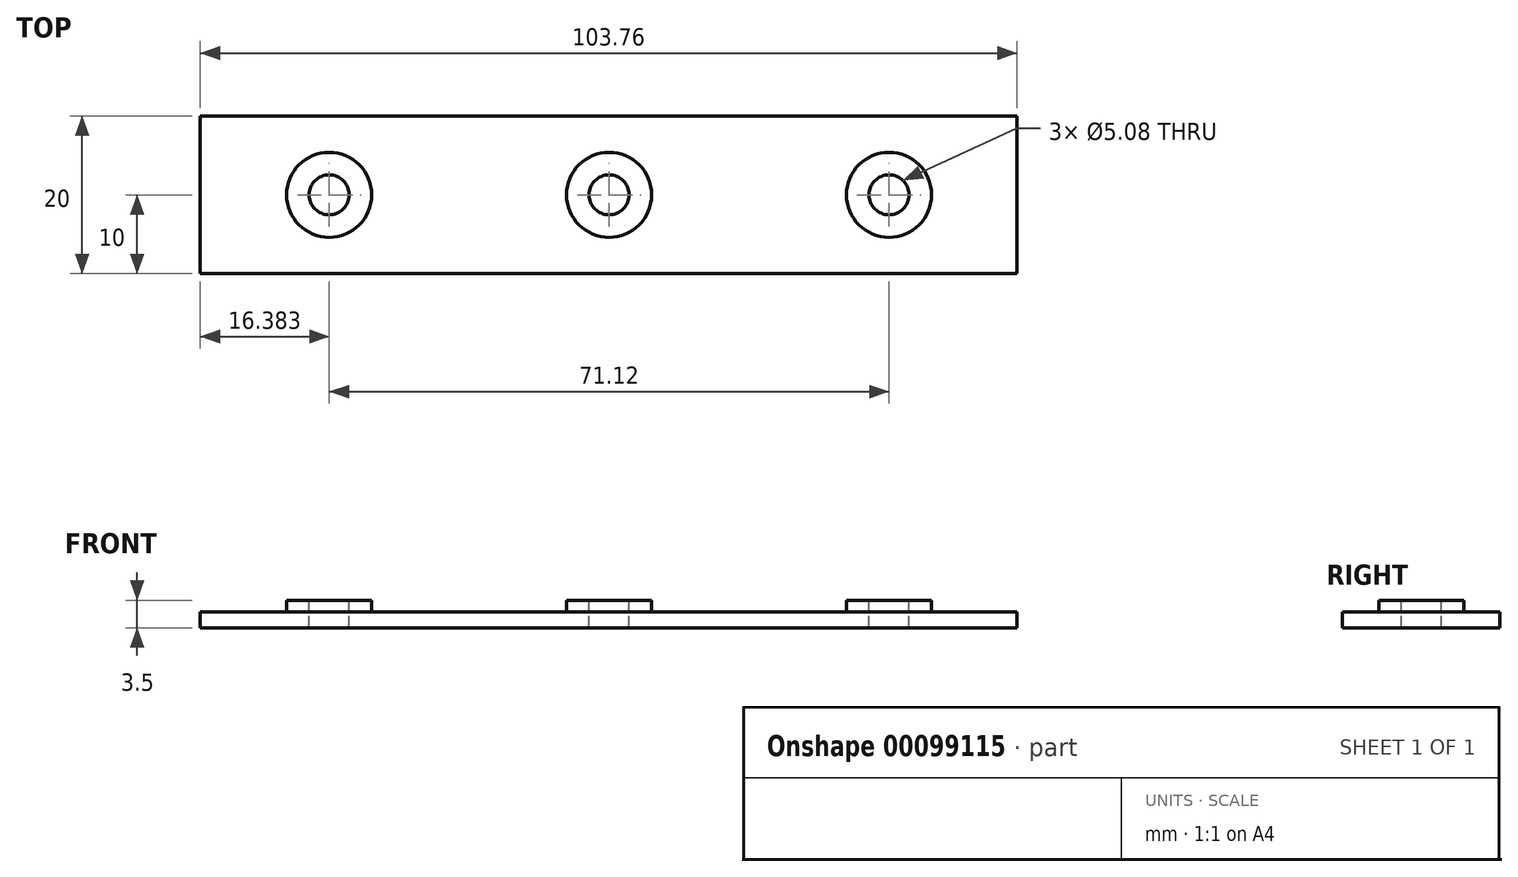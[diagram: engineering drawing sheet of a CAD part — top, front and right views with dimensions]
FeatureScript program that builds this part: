
annotation { "Feature Type Name" : "Feature", "Feature Type Description" : "" }
export const myFeature = defineFeature(function(context is Context, id is Id, definition is map)
    precondition{}
    {
        {
            var Q0;
            Q0=qCreatedBy(makeId("Right.planeOp"),FACE);
            var sketch = newSketch(context, id + "F0", { "sketchPlane" : qUnion([Q0])});
            skLineSegment(sketch, "E0", {"start": v(0, 0) * mm, "end": v(0, 2) * mm});
            skLineSegment(sketch, "E1", {"start": v(0, 0) * mm, "end": v(20, 0) * mm});
            skLineSegment(sketch, "E2", {"start": v(20, 0) * mm, "end": v(20, 2) * mm});
            skLineSegment(sketch, "E3", {"start": v(20, 2) * mm, "end": v(0, 2) * mm});
            skSolve(sketch);
        }
        {
            var Q0;
            Q0=makeQuery(id+"F0.imprint","IMPRINT",FACE,{"disambiguationData":[TD([[makeQuery(id+"F0.imprint","IMPRINT",EDGE,{"derivedFrom":sQuery(id+"F0.wireOp",EDGE,"E0")}),-1.0]])]});
            extrude(context, id + "F1", {"entities" : qUnion([Q0]), "depth" : 103.76 * mm});
        }
        {
            var Q0;
            Q0=makeQuery(id+"F1.opExtrude","SWEPT_FACE",FACE,{"disambiguationData":[OSD([sQuery(id+"F0.wireOp",EDGE,"E1")])]});
            var sketch = newSketch(context, id + "F2", { "sketchPlane" : qUnion([Q0])});
            skCircle(sketch, "E4", {"center": v(87.5, -10) * mm, "radius": 2.54 * mm});
            skCircle(sketch, "E5", {"center": v(16.38, -10) * mm, "radius": 2.54 * mm});
            skLineSegment(sketch, "E6", {"start": v(16.38, -10) * mm, "end": v(0, -10) * mm, "construction": true});
            skPoint(sketch, "E6.endSnap0", {"position": v(0, -10) * mm});
            skCircle(sketch, "E7", {"center": v(51.94, -10) * mm, "radius": 2.54 * mm});
            skSolve(sketch);
        }
        {
            var Q0;
            Q0=qSketchRegion(id+"F2",true);
            extrude(context, id + "F3", {"entities" : qUnion([Q0]), "operationType" : NewBodyOperationType.REMOVE, "endBound" : BoundingType.SYMMETRIC, "depth" : 25.4 * mm, "offsetDistance" : 25.4 * mm});
        }
        {
            var Q0;
            Q0=makeQuery(id+"F1.opExtrude","SWEPT_FACE",FACE,{"disambiguationData":[OSD([sQuery(id+"F0.wireOp",EDGE,"E3")])]});
            var sketch = newSketch(context, id + "F4", { "sketchPlane" : qUnion([Q0])});
            skCircle(sketch, "E8", {"center": v(16.38, 10) * mm, "radius": 5.4 * mm});
            skCircle(sketch, "E9", {"center": v(16.38, 10) * mm, "radius": 2.54 * mm});
            skCircle(sketch, "E10", {"center": v(51.94, 10) * mm, "radius": 5.4 * mm});
            skCircle(sketch, "E11", {"center": v(51.94, 10) * mm, "radius": 2.54 * mm});
            skCircle(sketch, "E12", {"center": v(87.5, 10) * mm, "radius": 2.54 * mm});
            skCircle(sketch, "E13", {"center": v(87.5, 10) * mm, "radius": 5.4 * mm});
            skSolve(sketch);
        }
        {
            var Q0;
            Q0 = qSketchRegion(id + "F4", true);
            extrude(context, id + "F5", {"entities" : qUnion([Q0]), "operationType" : NewBodyOperationType.ADD, "depth" : 1.5 * mm, "offsetDistance" : 25.4 * mm});
        }
    });
